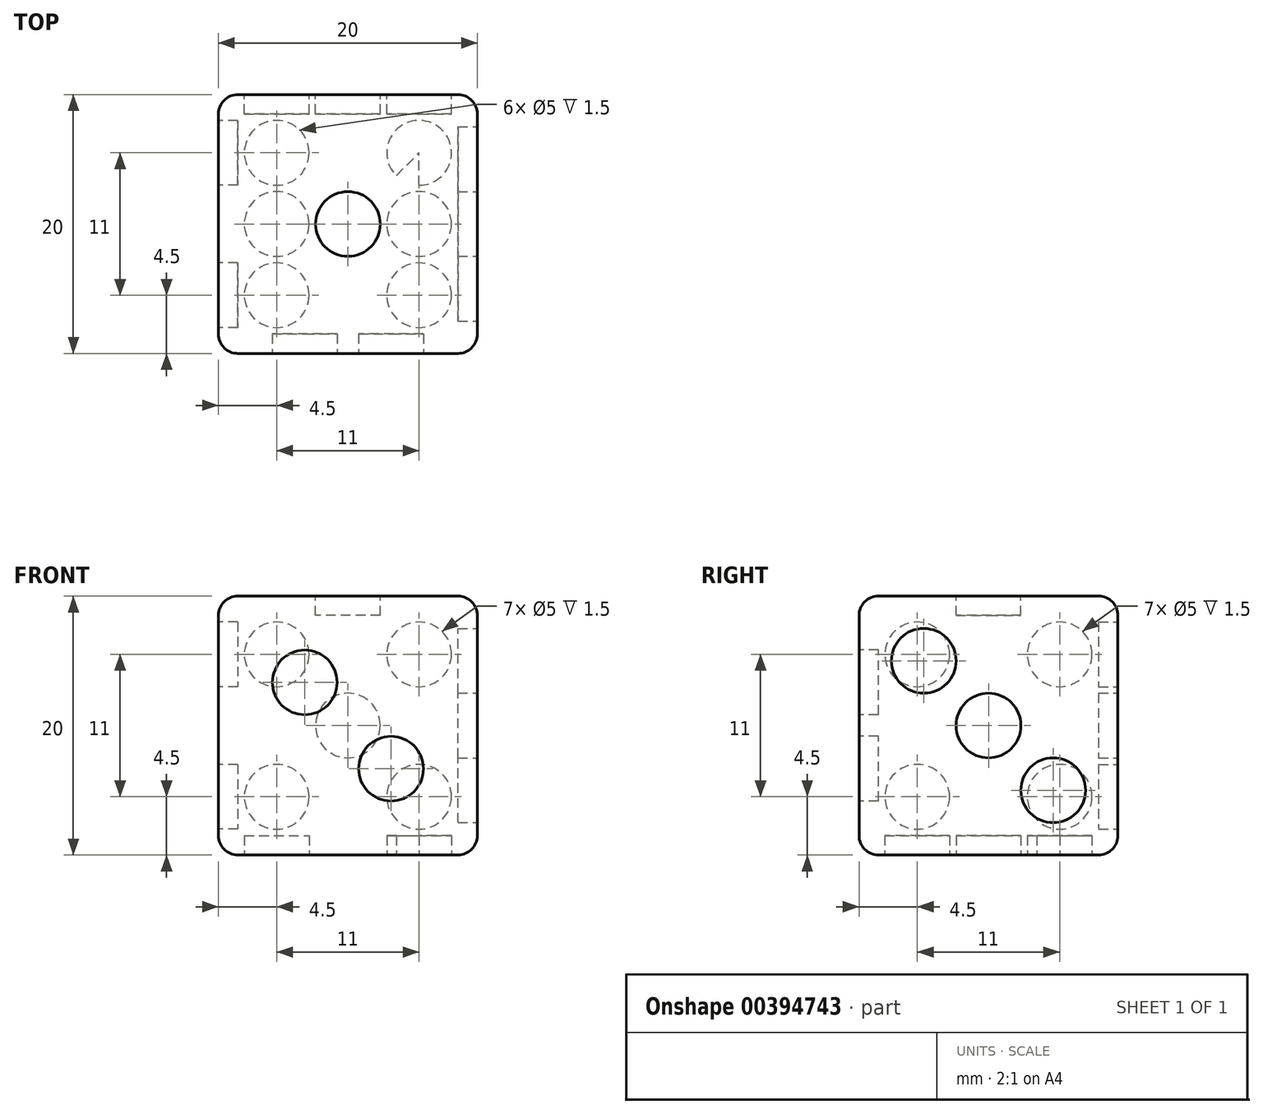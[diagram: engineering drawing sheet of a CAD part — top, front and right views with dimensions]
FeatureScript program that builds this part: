
annotation { "Feature Type Name" : "Feature", "Feature Type Description" : "" }
export const myFeature = defineFeature(function(context is Context, id is Id, definition is map)
    precondition{}
    {
        {
            assignVariable(context, id + "F0", {"name" : "Extrude", "anyValue" : -1.5});
        }
        {
            var Q0;
            Q0=qCreatedBy(makeId("Top.planeOp"),FACE);
            var sketch = newSketch(context, id + "F1", { "sketchPlane" : qUnion([Q0])});
            skLineSegment(sketch, "E0.bottom", {"start": v(-10, 10) * mm, "end": v(10, 10) * mm});
            skLineSegment(sketch, "E0.top", {"start": v(-10, -10) * mm, "end": v(10, -10) * mm});
            skLineSegment(sketch, "E0.left", {"start": v(-10, 10) * mm, "end": v(-10, -10) * mm});
            skLineSegment(sketch, "E0.right", {"start": v(10, 10) * mm, "end": v(10, -10) * mm});
            skPoint(sketch, "E0.middle", {"position": v(0, 0) * mm});
            skSolve(sketch);
        }
        {
            var Q0;
            Q0=makeQuery(id+"F1.imprint","IMPRINT",FACE,{"disambiguationData":[TD([[makeQuery(id+"F1.imprint","IMPRINT",EDGE,{"derivedFrom":sQuery(id+"F1.wireOp",EDGE,"E0.bottom")}),-1.0]])]});
            extrude(context, id + "F2", {"entities" : qUnion([Q0]), "depth" : 20 * mm});
        }
        {
            var Q0;
            Q0=makeQuery(id+"F2.opExtrude","CAP_FACE",FACE,{"disambiguationData":[OSD([sQuery(id+"F1.wireOp",EDGE,"E0.bottom"),sQuery(id+"F1.wireOp",EDGE,"E0.top"),sQuery(id+"F1.wireOp",EDGE,"E0.left"),sQuery(id+"F1.wireOp",EDGE,"E0.right")])],"isStart":false});
            var sketch = newSketch(context, id + "F3", { "sketchPlane" : qUnion([Q0])});
            skCircle(sketch, "E1", {"center": v(0, 0) * mm, "radius": 2.5 * mm});
            skSolve(sketch);
        }
        {
            var Q0;
            Q0=makeQuery(id+"F2.opExtrude","CAP_FACE",FACE,{"disambiguationData":[OSD([sQuery(id+"F1.wireOp",EDGE,"E0.bottom"),sQuery(id+"F1.wireOp",EDGE,"E0.top"),sQuery(id+"F1.wireOp",EDGE,"E0.left"),sQuery(id+"F1.wireOp",EDGE,"E0.right")])],"isStart":true});
            var sketch = newSketch(context, id + "F4", { "sketchPlane" : qUnion([Q0])});
            skCircle(sketch, "E2", {"center": v(-5.5, 5.5) * mm, "radius": 2.5 * mm});
            skCircle(sketch, "E3", {"center": v(-5.5, -5.5) * mm, "radius": 2.5 * mm});
            skCircle(sketch, "E4", {"center": v(-5.5, 0) * mm, "radius": 2.5 * mm});
            skCircle(sketch, "E5", {"center": v(5.5, 5.5) * mm, "radius": 2.5 * mm});
            skCircle(sketch, "E6", {"center": v(5.5, 0) * mm, "radius": 2.5 * mm});
            skCircle(sketch, "E7", {"center": v(5.5, -5.5) * mm, "radius": 2.5 * mm});
            skLineSegment(sketch, "E8", {"start": v(10, 10) * mm, "end": v(-10, -10) * mm});
            skLineSegment(sketch, "E9", {"start": v(-10, 10) * mm, "end": v(10, -10) * mm});
            skLineSegment(sketch, "E10", {"start": v(-5.5, 5.5) * mm, "end": v(-5.5, -5.5) * mm});
            skLineSegment(sketch, "E11", {"start": v(5.5, 5.5) * mm, "end": v(5.5, -5.5) * mm});
            skSolve(sketch);
        }
        {
            var Q0;
            Q0=makeQuery(id+"F2.opExtrude","SWEPT_FACE",FACE,{"disambiguationData":[OSD([sQuery(id+"F1.wireOp",EDGE,"E0.bottom")])]});
            var sketch = newSketch(context, id + "F5", { "sketchPlane" : qUnion([Q0])});
            skLineSegment(sketch, "E12", {"start": v(10, 20) * mm, "end": v(-10, 0) * mm});
            skLineSegment(sketch, "E13", {"start": v(-10, 20) * mm, "end": v(10, 0) * mm});
            skCircle(sketch, "E14", {"center": v(0, 10) * mm, "radius": 2.5 * mm});
            skCircle(sketch, "E15", {"center": v(-5.5, 15.5) * mm, "radius": 2.5 * mm});
            skCircle(sketch, "E16", {"center": v(5.5, 15.5) * mm, "radius": 2.5 * mm});
            skCircle(sketch, "E17", {"center": v(5.5, 4.5) * mm, "radius": 2.5 * mm});
            skCircle(sketch, "E18", {"center": v(-5.5, 4.5) * mm, "radius": 2.5 * mm});
            skLineSegment(sketch, "E19.bottom", {"start": v(-5.5, 15.5) * mm, "end": v(5.5, 15.5) * mm});
            skLineSegment(sketch, "E19.top", {"start": v(-5.5, 4.5) * mm, "end": v(5.5, 4.5) * mm});
            skLineSegment(sketch, "E19.left", {"start": v(-5.5, 15.5) * mm, "end": v(-5.5, 4.5) * mm});
            skLineSegment(sketch, "E19.right", {"start": v(5.5, 15.5) * mm, "end": v(5.5, 4.5) * mm});
            skSolve(sketch);
        }
        {
            var Q0;
            Q0=makeQuery(id+"F2.opExtrude","SWEPT_FACE",FACE,{"disambiguationData":[OSD([sQuery(id+"F1.wireOp",EDGE,"E0.top")])]});
            var sketch = newSketch(context, id + "F6", { "sketchPlane" : qUnion([Q0])});
            skLineSegment(sketch, "E20", {"start": v(-10, 20) * mm, "end": v(-3.33, 13.33) * mm});
            skLineSegment(sketch, "E21", {"start": v(-3.33, 13.33) * mm, "end": v(3.33, 6.67) * mm});
            skLineSegment(sketch, "E22", {"start": v(3.33, 6.67) * mm, "end": v(10, 0) * mm});
            skCircle(sketch, "E23", {"center": v(-3.33, 13.33) * mm, "radius": 2.5 * mm});
            skCircle(sketch, "E24", {"center": v(3.33, 6.67) * mm, "radius": 2.5 * mm});
            skSolve(sketch);
        }
        {
            var Q0;
            Q0=makeQuery(id+"F2.opExtrude","SWEPT_FACE",FACE,{"disambiguationData":[OSD([sQuery(id+"F1.wireOp",EDGE,"E0.left")])]});
            var sketch = newSketch(context, id + "F7", { "sketchPlane" : qUnion([Q0])});
            skLineSegment(sketch, "E25", {"start": v(-10, 20) * mm, "end": v(10, 0) * mm});
            skLineSegment(sketch, "E26", {"start": v(10, 20) * mm, "end": v(-10, 0) * mm});
            skCircle(sketch, "E27", {"center": v(-5.5, 15.5) * mm, "radius": 2.5 * mm});
            skCircle(sketch, "E28", {"center": v(5.5, 15.5) * mm, "radius": 2.5 * mm});
            skCircle(sketch, "E29", {"center": v(5.5, 4.5) * mm, "radius": 2.5 * mm});
            skCircle(sketch, "E30", {"center": v(-5.5, 4.5) * mm, "radius": 2.5 * mm});
            skLineSegment(sketch, "E31.bottom", {"start": v(-5.5, 15.5) * mm, "end": v(5.5, 15.5) * mm});
            skLineSegment(sketch, "E31.top", {"start": v(-5.5, 4.5) * mm, "end": v(5.5, 4.5) * mm});
            skLineSegment(sketch, "E31.left", {"start": v(-5.5, 15.5) * mm, "end": v(-5.5, 4.5) * mm});
            skLineSegment(sketch, "E31.right", {"start": v(5.5, 15.5) * mm, "end": v(5.5, 4.5) * mm});
            skSolve(sketch);
        }
        {
            var Q0;
            Q0=makeQuery(id+"F2.opExtrude","SWEPT_FACE",FACE,{"disambiguationData":[OSD([sQuery(id+"F1.wireOp",EDGE,"E0.right")])]});
            var sketch = newSketch(context, id + "F8", { "sketchPlane" : qUnion([Q0])});
            skLineSegment(sketch, "E32", {"start": v(-10, 20) * mm, "end": v(-5, 15) * mm});
            skLineSegment(sketch, "E33", {"start": v(-5, 15) * mm, "end": v(0, 10) * mm});
            skLineSegment(sketch, "E34", {"start": v(0, 10) * mm, "end": v(5, 5) * mm});
            skLineSegment(sketch, "E35", {"start": v(5, 5) * mm, "end": v(10, 0) * mm});
            skCircle(sketch, "E36", {"center": v(-5, 15) * mm, "radius": 2.5 * mm});
            skCircle(sketch, "E37", {"center": v(0, 10) * mm, "radius": 2.5 * mm});
            skCircle(sketch, "E38", {"center": v(5, 5) * mm, "radius": 2.5 * mm});
            skSolve(sketch);
        }
        {
            var Q0;
            Q0=makeQuery(id+"F3.imprint","IMPRINT",FACE,{"disambiguationData":[TD([[makeQuery(id+"F3.imprint","IMPRINT",EDGE,{"derivedFrom":sQuery(id+"F3.wireOp",EDGE,"E1")}),1.0]])]});
            extrude(context, id + "F9", {"entities" : qUnion([Q0]), "operationType" : NewBodyOperationType.REMOVE, "depth" : (getVariable(context, 'Extrude')) * mm});
        }
        {
            var Q0;
            {var subQ0=sQuery(id+"F6.wireOp",EDGE,"E21");var subQ1=sQuery(id+"F6.wireOp",EDGE,"E20");var subQ2=makeQuery(id+"F6.imprint","INTERSECT",VERTEX,{"derivedFrom":[subQ1,subQ0]});Q0=makeQuery(id+"F6.imprint","IMPRINT",FACE,{"disambiguationData":[TD([[makeQuery(id+"F6.imprint","IMPRINT",EDGE,{"disambiguationData":[TD([[subQ2,1.0]])],"derivedFrom":subQ1}),1.0]])]});}
            var Q1;
            {var subQ0=sQuery(id+"F6.wireOp",EDGE,"E21");var subQ1=sQuery(id+"F6.wireOp",EDGE,"E20");var subQ2=makeQuery(id+"F6.imprint","INTERSECT",VERTEX,{"derivedFrom":[subQ1,subQ0]});Q1=makeQuery(id+"F6.imprint","IMPRINT",FACE,{"disambiguationData":[TD([[makeQuery(id+"F6.imprint","IMPRINT",EDGE,{"disambiguationData":[TD([[subQ2,1.0]])],"derivedFrom":subQ1}),-1.0]])]});}
            var Q2;
            {var subQ0=sQuery(id+"F6.wireOp",EDGE,"E22");var subQ1=sQuery(id+"F6.wireOp",EDGE,"E21");var subQ2=makeQuery(id+"F6.imprint","INTERSECT",VERTEX,{"derivedFrom":[subQ1,subQ0]});Q2=makeQuery(id+"F6.imprint","IMPRINT",FACE,{"disambiguationData":[TD([[makeQuery(id+"F6.imprint","IMPRINT",EDGE,{"disambiguationData":[TD([[subQ2,1.0]])],"derivedFrom":subQ1}),-1.0]])]});}
            var Q3;
            {var subQ0=sQuery(id+"F6.wireOp",EDGE,"E22");var subQ1=sQuery(id+"F6.wireOp",EDGE,"E21");var subQ2=makeQuery(id+"F6.imprint","INTERSECT",VERTEX,{"derivedFrom":[subQ1,subQ0]});Q3=makeQuery(id+"F6.imprint","IMPRINT",FACE,{"disambiguationData":[TD([[makeQuery(id+"F6.imprint","IMPRINT",EDGE,{"disambiguationData":[TD([[subQ2,1.0]])],"derivedFrom":subQ1}),1.0]])]});}
            extrude(context, id + "F10", {"entities" : qUnion([Q0, Q1, Q2, Q3]), "operationType" : NewBodyOperationType.REMOVE, "depth" : (getVariable(context, 'Extrude')) * mm});
        }
        {
            var Q0;
            {var subQ0=sQuery(id+"F8.wireOp",EDGE,"E33");var subQ1=sQuery(id+"F8.wireOp",EDGE,"E32");var subQ2=makeQuery(id+"F8.imprint","INTERSECT",VERTEX,{"derivedFrom":[subQ1,subQ0]});Q0=makeQuery(id+"F8.imprint","IMPRINT",FACE,{"disambiguationData":[TD([[makeQuery(id+"F8.imprint","IMPRINT",EDGE,{"disambiguationData":[TD([[subQ2,1.0]])],"derivedFrom":subQ1}),1.0]])]});}
            var Q1;
            {var subQ0=sQuery(id+"F8.wireOp",EDGE,"E33");var subQ1=sQuery(id+"F8.wireOp",EDGE,"E32");var subQ2=makeQuery(id+"F8.imprint","INTERSECT",VERTEX,{"derivedFrom":[subQ1,subQ0]});Q1=makeQuery(id+"F8.imprint","IMPRINT",FACE,{"disambiguationData":[TD([[makeQuery(id+"F8.imprint","IMPRINT",EDGE,{"disambiguationData":[TD([[subQ2,1.0]])],"derivedFrom":subQ1}),-1.0]])]});}
            var Q2;
            {var subQ0=sQuery(id+"F8.wireOp",EDGE,"E34");var subQ1=sQuery(id+"F8.wireOp",EDGE,"E33");var subQ2=makeQuery(id+"F8.imprint","INTERSECT",VERTEX,{"derivedFrom":[subQ1,subQ0]});Q2=makeQuery(id+"F8.imprint","IMPRINT",FACE,{"disambiguationData":[TD([[makeQuery(id+"F8.imprint","IMPRINT",EDGE,{"disambiguationData":[TD([[subQ2,1.0]])],"derivedFrom":subQ1}),-1.0]])]});}
            var Q3;
            {var subQ0=sQuery(id+"F8.wireOp",EDGE,"E34");var subQ1=sQuery(id+"F8.wireOp",EDGE,"E33");var subQ2=makeQuery(id+"F8.imprint","INTERSECT",VERTEX,{"derivedFrom":[subQ1,subQ0]});Q3=makeQuery(id+"F8.imprint","IMPRINT",FACE,{"disambiguationData":[TD([[makeQuery(id+"F8.imprint","IMPRINT",EDGE,{"disambiguationData":[TD([[subQ2,1.0]])],"derivedFrom":subQ1}),1.0]])]});}
            var Q4;
            {var subQ0=sQuery(id+"F8.wireOp",EDGE,"E35");var subQ1=sQuery(id+"F8.wireOp",EDGE,"E34");var subQ2=makeQuery(id+"F8.imprint","INTERSECT",VERTEX,{"derivedFrom":[subQ1,subQ0]});Q4=makeQuery(id+"F8.imprint","IMPRINT",FACE,{"disambiguationData":[TD([[makeQuery(id+"F8.imprint","IMPRINT",EDGE,{"disambiguationData":[TD([[subQ2,1.0]])],"derivedFrom":subQ1}),1.0]])]});}
            var Q5;
            {var subQ0=sQuery(id+"F8.wireOp",EDGE,"E35");var subQ1=sQuery(id+"F8.wireOp",EDGE,"E34");var subQ2=makeQuery(id+"F8.imprint","INTERSECT",VERTEX,{"derivedFrom":[subQ1,subQ0]});Q5=makeQuery(id+"F8.imprint","IMPRINT",FACE,{"disambiguationData":[TD([[makeQuery(id+"F8.imprint","IMPRINT",EDGE,{"disambiguationData":[TD([[subQ2,1.0]])],"derivedFrom":subQ1}),-1.0]])]});}
            extrude(context, id + "F11", {"entities" : qUnion([Q0, Q1, Q2, Q3, Q4, Q5]), "operationType" : NewBodyOperationType.REMOVE, "depth" : (getVariable(context, 'Extrude')) * mm});
        }
        {
            var Q0;
            {var subQ1=sQuery(id+"F7.wireOp",EDGE,"E25");var subQ3=sQuery(id+"F7.wireOp",EDGE,"E29");var subQ4=makeQuery(id+"F7.imprint","INTERSECT",VERTEX,{"disambiguationData":[OD(1.0)],"derivedFrom":[subQ1,subQ3]});Q0=makeQuery(id+"F7.imprint","IMPRINT",FACE,{"disambiguationData":[TD([[makeQuery(id+"F7.imprint","IMPRINT",EDGE,{"disambiguationData":[TD([[subQ4,1.0]])],"derivedFrom":subQ3}),1.0]])]});}
            var Q1;
            {var subQ1=sQuery(id+"F7.wireOp",EDGE,"E25");var subQ3=sQuery(id+"F7.wireOp",EDGE,"E29");var subQ4=makeQuery(id+"F7.imprint","INTERSECT",VERTEX,{"disambiguationData":[OD(0.0)],"derivedFrom":[subQ1,subQ3]});Q1=makeQuery(id+"F7.imprint","IMPRINT",FACE,{"disambiguationData":[TD([[makeQuery(id+"F7.imprint","IMPRINT",EDGE,{"disambiguationData":[TD([[subQ4,-1.0]])],"derivedFrom":subQ3}),1.0]])]});}
            var Q2;
            {var subQ1=sQuery(id+"F7.wireOp",EDGE,"E25");var subQ3=sQuery(id+"F7.wireOp",EDGE,"E29");var subQ4=makeQuery(id+"F7.imprint","INTERSECT",VERTEX,{"disambiguationData":[OD(0.0)],"derivedFrom":[subQ1,subQ3]});Q2=makeQuery(id+"F7.imprint","IMPRINT",FACE,{"disambiguationData":[TD([[makeQuery(id+"F7.imprint","IMPRINT",EDGE,{"disambiguationData":[TD([[subQ4,1.0]])],"derivedFrom":subQ3}),1.0]])]});}
            var Q3;
            {var subQ1=sQuery(id+"F7.wireOp",EDGE,"E25");var subQ3=sQuery(id+"F7.wireOp",EDGE,"E29");var subQ4=makeQuery(id+"F7.imprint","INTERSECT",VERTEX,{"disambiguationData":[OD(1.0)],"derivedFrom":[subQ1,subQ3]});Q3=makeQuery(id+"F7.imprint","IMPRINT",FACE,{"disambiguationData":[TD([[makeQuery(id+"F7.imprint","IMPRINT",EDGE,{"disambiguationData":[TD([[subQ4,-1.0]])],"derivedFrom":subQ3}),1.0]])]});}
            var Q4;
            {var subQ1=sQuery(id+"F7.wireOp",EDGE,"E26");var subQ3=sQuery(id+"F7.wireOp",EDGE,"E30");var subQ4=makeQuery(id+"F7.imprint","INTERSECT",VERTEX,{"disambiguationData":[OD(1.0)],"derivedFrom":[subQ1,subQ3]});Q4=makeQuery(id+"F7.imprint","IMPRINT",FACE,{"disambiguationData":[TD([[makeQuery(id+"F7.imprint","IMPRINT",EDGE,{"disambiguationData":[TD([[subQ4,1.0]])],"derivedFrom":subQ3}),1.0]])]});}
            var Q5;
            {var subQ1=sQuery(id+"F7.wireOp",EDGE,"E26");var subQ3=sQuery(id+"F7.wireOp",EDGE,"E30");var subQ4=makeQuery(id+"F7.imprint","INTERSECT",VERTEX,{"disambiguationData":[OD(1.0)],"derivedFrom":[subQ1,subQ3]});Q5=makeQuery(id+"F7.imprint","IMPRINT",FACE,{"disambiguationData":[TD([[makeQuery(id+"F7.imprint","IMPRINT",EDGE,{"disambiguationData":[TD([[subQ4,-1.0]])],"derivedFrom":subQ3}),1.0]])]});}
            var Q6;
            {var subQ1=sQuery(id+"F7.wireOp",EDGE,"E26");var subQ3=sQuery(id+"F7.wireOp",EDGE,"E30");var subQ4=makeQuery(id+"F7.imprint","INTERSECT",VERTEX,{"disambiguationData":[OD(0.0)],"derivedFrom":[subQ1,subQ3]});Q6=makeQuery(id+"F7.imprint","IMPRINT",FACE,{"disambiguationData":[TD([[makeQuery(id+"F7.imprint","IMPRINT",EDGE,{"disambiguationData":[TD([[subQ4,1.0]])],"derivedFrom":subQ3}),1.0]])]});}
            var Q7;
            {var subQ1=sQuery(id+"F7.wireOp",EDGE,"E26");var subQ3=sQuery(id+"F7.wireOp",EDGE,"E30");var subQ4=makeQuery(id+"F7.imprint","INTERSECT",VERTEX,{"disambiguationData":[OD(0.0)],"derivedFrom":[subQ1,subQ3]});Q7=makeQuery(id+"F7.imprint","IMPRINT",FACE,{"disambiguationData":[TD([[makeQuery(id+"F7.imprint","IMPRINT",EDGE,{"disambiguationData":[TD([[subQ4,-1.0]])],"derivedFrom":subQ3}),1.0]])]});}
            var Q8;
            {var subQ1=sQuery(id+"F7.wireOp",EDGE,"E25");var subQ3=sQuery(id+"F7.wireOp",EDGE,"E27");var subQ4=makeQuery(id+"F7.imprint","INTERSECT",VERTEX,{"disambiguationData":[OD(1.0)],"derivedFrom":[subQ1,subQ3]});Q8=makeQuery(id+"F7.imprint","IMPRINT",FACE,{"disambiguationData":[TD([[makeQuery(id+"F7.imprint","IMPRINT",EDGE,{"disambiguationData":[TD([[subQ4,1.0]])],"derivedFrom":subQ3}),1.0]])]});}
            var Q9;
            {var subQ1=sQuery(id+"F7.wireOp",EDGE,"E25");var subQ3=sQuery(id+"F7.wireOp",EDGE,"E27");var subQ4=makeQuery(id+"F7.imprint","INTERSECT",VERTEX,{"disambiguationData":[OD(0.0)],"derivedFrom":[subQ1,subQ3]});Q9=makeQuery(id+"F7.imprint","IMPRINT",FACE,{"disambiguationData":[TD([[makeQuery(id+"F7.imprint","IMPRINT",EDGE,{"disambiguationData":[TD([[subQ4,-1.0]])],"derivedFrom":subQ3}),1.0]])]});}
            var Q10;
            {var subQ1=sQuery(id+"F7.wireOp",EDGE,"E25");var subQ3=sQuery(id+"F7.wireOp",EDGE,"E27");var subQ4=makeQuery(id+"F7.imprint","INTERSECT",VERTEX,{"disambiguationData":[OD(0.0)],"derivedFrom":[subQ1,subQ3]});Q10=makeQuery(id+"F7.imprint","IMPRINT",FACE,{"disambiguationData":[TD([[makeQuery(id+"F7.imprint","IMPRINT",EDGE,{"disambiguationData":[TD([[subQ4,1.0]])],"derivedFrom":subQ3}),1.0]])]});}
            var Q11;
            {var subQ1=sQuery(id+"F7.wireOp",EDGE,"E25");var subQ3=sQuery(id+"F7.wireOp",EDGE,"E27");var subQ4=makeQuery(id+"F7.imprint","INTERSECT",VERTEX,{"disambiguationData":[OD(1.0)],"derivedFrom":[subQ1,subQ3]});Q11=makeQuery(id+"F7.imprint","IMPRINT",FACE,{"disambiguationData":[TD([[makeQuery(id+"F7.imprint","IMPRINT",EDGE,{"disambiguationData":[TD([[subQ4,-1.0]])],"derivedFrom":subQ3}),1.0]])]});}
            var Q12;
            {var subQ1=sQuery(id+"F7.wireOp",EDGE,"E26");var subQ3=sQuery(id+"F7.wireOp",EDGE,"E28");var subQ4=makeQuery(id+"F7.imprint","INTERSECT",VERTEX,{"disambiguationData":[OD(1.0)],"derivedFrom":[subQ1,subQ3]});Q12=makeQuery(id+"F7.imprint","IMPRINT",FACE,{"disambiguationData":[TD([[makeQuery(id+"F7.imprint","IMPRINT",EDGE,{"disambiguationData":[TD([[subQ4,-1.0]])],"derivedFrom":subQ3}),1.0]])]});}
            var Q13;
            {var subQ1=sQuery(id+"F7.wireOp",EDGE,"E26");var subQ3=sQuery(id+"F7.wireOp",EDGE,"E28");var subQ4=makeQuery(id+"F7.imprint","INTERSECT",VERTEX,{"disambiguationData":[OD(0.0)],"derivedFrom":[subQ1,subQ3]});Q13=makeQuery(id+"F7.imprint","IMPRINT",FACE,{"disambiguationData":[TD([[makeQuery(id+"F7.imprint","IMPRINT",EDGE,{"disambiguationData":[TD([[subQ4,1.0]])],"derivedFrom":subQ3}),1.0]])]});}
            var Q14;
            {var subQ1=sQuery(id+"F7.wireOp",EDGE,"E26");var subQ3=sQuery(id+"F7.wireOp",EDGE,"E28");var subQ4=makeQuery(id+"F7.imprint","INTERSECT",VERTEX,{"disambiguationData":[OD(1.0)],"derivedFrom":[subQ1,subQ3]});Q14=makeQuery(id+"F7.imprint","IMPRINT",FACE,{"disambiguationData":[TD([[makeQuery(id+"F7.imprint","IMPRINT",EDGE,{"disambiguationData":[TD([[subQ4,1.0]])],"derivedFrom":subQ3}),1.0]])]});}
            var Q15;
            {var subQ1=sQuery(id+"F7.wireOp",EDGE,"E26");var subQ3=sQuery(id+"F7.wireOp",EDGE,"E28");var subQ4=makeQuery(id+"F7.imprint","INTERSECT",VERTEX,{"disambiguationData":[OD(0.0)],"derivedFrom":[subQ1,subQ3]});Q15=makeQuery(id+"F7.imprint","IMPRINT",FACE,{"disambiguationData":[TD([[makeQuery(id+"F7.imprint","IMPRINT",EDGE,{"disambiguationData":[TD([[subQ4,-1.0]])],"derivedFrom":subQ3}),1.0]])]});}
            extrude(context, id + "F12", {"entities" : qUnion([Q0, Q1, Q2, Q3, Q4, Q5, Q6, Q7, Q8, Q9, Q10, Q11, Q12, Q13, Q14, Q15]), "operationType" : NewBodyOperationType.REMOVE, "depth" : (getVariable(context, 'Extrude')) * mm});
        }
        {
            var Q0;
            {var subQ1=sQuery(id+"F5.wireOp",EDGE,"E12");var subQ3=sQuery(id+"F5.wireOp",EDGE,"E18");var subQ4=makeQuery(id+"F5.imprint","INTERSECT",VERTEX,{"disambiguationData":[OD(1.0)],"derivedFrom":[subQ1,subQ3]});Q0=makeQuery(id+"F5.imprint","IMPRINT",FACE,{"disambiguationData":[TD([[makeQuery(id+"F5.imprint","IMPRINT",EDGE,{"disambiguationData":[TD([[subQ4,1.0]])],"derivedFrom":subQ3}),1.0]])]});}
            var Q1;
            {var subQ1=sQuery(id+"F5.wireOp",EDGE,"E12");var subQ3=sQuery(id+"F5.wireOp",EDGE,"E18");var subQ4=makeQuery(id+"F5.imprint","INTERSECT",VERTEX,{"disambiguationData":[OD(1.0)],"derivedFrom":[subQ1,subQ3]});Q1=makeQuery(id+"F5.imprint","IMPRINT",FACE,{"disambiguationData":[TD([[makeQuery(id+"F5.imprint","IMPRINT",EDGE,{"disambiguationData":[TD([[subQ4,-1.0]])],"derivedFrom":subQ3}),1.0]])]});}
            var Q2;
            {var subQ1=sQuery(id+"F5.wireOp",EDGE,"E12");var subQ3=sQuery(id+"F5.wireOp",EDGE,"E18");var subQ4=makeQuery(id+"F5.imprint","INTERSECT",VERTEX,{"disambiguationData":[OD(0.0)],"derivedFrom":[subQ1,subQ3]});Q2=makeQuery(id+"F5.imprint","IMPRINT",FACE,{"disambiguationData":[TD([[makeQuery(id+"F5.imprint","IMPRINT",EDGE,{"disambiguationData":[TD([[subQ4,1.0]])],"derivedFrom":subQ3}),1.0]])]});}
            var Q3;
            {var subQ1=sQuery(id+"F5.wireOp",EDGE,"E12");var subQ3=sQuery(id+"F5.wireOp",EDGE,"E18");var subQ4=makeQuery(id+"F5.imprint","INTERSECT",VERTEX,{"disambiguationData":[OD(0.0)],"derivedFrom":[subQ1,subQ3]});Q3=makeQuery(id+"F5.imprint","IMPRINT",FACE,{"disambiguationData":[TD([[makeQuery(id+"F5.imprint","IMPRINT",EDGE,{"disambiguationData":[TD([[subQ4,-1.0]])],"derivedFrom":subQ3}),1.0]])]});}
            var Q4;
            {var subQ0=sQuery(id+"F5.wireOp",EDGE,"E13");var subQ1=sQuery(id+"F5.wireOp",EDGE,"E12");var subQ2=makeQuery(id+"F5.imprint","INTERSECT",VERTEX,{"derivedFrom":[subQ1,subQ0]});Q4=makeQuery(id+"F5.imprint","IMPRINT",FACE,{"disambiguationData":[TD([[makeQuery(id+"F5.imprint","IMPRINT",EDGE,{"disambiguationData":[TD([[subQ2,-1.0]])],"derivedFrom":subQ1}),1.0]])]});}
            var Q5;
            {var subQ0=sQuery(id+"F5.wireOp",EDGE,"E14");var subQ1=sQuery(id+"F5.wireOp",EDGE,"E12");var subQ2=makeQuery(id+"F5.imprint","INTERSECT",VERTEX,{"disambiguationData":[OD(0.0)],"derivedFrom":[subQ1,subQ0]});Q5=makeQuery(id+"F5.imprint","IMPRINT",FACE,{"disambiguationData":[TD([[makeQuery(id+"F5.imprint","IMPRINT",EDGE,{"disambiguationData":[TD([[subQ2,-1.0]])],"derivedFrom":subQ1}),1.0]])]});}
            var Q6;
            {var subQ0=sQuery(id+"F5.wireOp",EDGE,"E14");var subQ1=sQuery(id+"F5.wireOp",EDGE,"E12");var subQ2=makeQuery(id+"F5.imprint","INTERSECT",VERTEX,{"disambiguationData":[OD(0.0)],"derivedFrom":[subQ1,subQ0]});Q6=makeQuery(id+"F5.imprint","IMPRINT",FACE,{"disambiguationData":[TD([[makeQuery(id+"F5.imprint","IMPRINT",EDGE,{"disambiguationData":[TD([[subQ2,-1.0]])],"derivedFrom":subQ1}),-1.0]])]});}
            var Q7;
            {var subQ0=sQuery(id+"F5.wireOp",EDGE,"E13");var subQ1=sQuery(id+"F5.wireOp",EDGE,"E12");var subQ2=makeQuery(id+"F5.imprint","INTERSECT",VERTEX,{"derivedFrom":[subQ1,subQ0]});Q7=makeQuery(id+"F5.imprint","IMPRINT",FACE,{"disambiguationData":[TD([[makeQuery(id+"F5.imprint","IMPRINT",EDGE,{"disambiguationData":[TD([[subQ2,-1.0]])],"derivedFrom":subQ1}),-1.0]])]});}
            var Q8;
            {var subQ1=sQuery(id+"F5.wireOp",EDGE,"E13");var subQ3=sQuery(id+"F5.wireOp",EDGE,"E17");var subQ4=makeQuery(id+"F5.imprint","INTERSECT",VERTEX,{"disambiguationData":[OD(0.0)],"derivedFrom":[subQ1,subQ3]});Q8=makeQuery(id+"F5.imprint","IMPRINT",FACE,{"disambiguationData":[TD([[makeQuery(id+"F5.imprint","IMPRINT",EDGE,{"disambiguationData":[TD([[subQ4,-1.0]])],"derivedFrom":subQ3}),1.0]])]});}
            var Q9;
            {var subQ1=sQuery(id+"F5.wireOp",EDGE,"E13");var subQ3=sQuery(id+"F5.wireOp",EDGE,"E17");var subQ4=makeQuery(id+"F5.imprint","INTERSECT",VERTEX,{"disambiguationData":[OD(1.0)],"derivedFrom":[subQ1,subQ3]});Q9=makeQuery(id+"F5.imprint","IMPRINT",FACE,{"disambiguationData":[TD([[makeQuery(id+"F5.imprint","IMPRINT",EDGE,{"disambiguationData":[TD([[subQ4,1.0]])],"derivedFrom":subQ3}),1.0]])]});}
            var Q10;
            {var subQ1=sQuery(id+"F5.wireOp",EDGE,"E13");var subQ3=sQuery(id+"F5.wireOp",EDGE,"E17");var subQ4=makeQuery(id+"F5.imprint","INTERSECT",VERTEX,{"disambiguationData":[OD(1.0)],"derivedFrom":[subQ1,subQ3]});Q10=makeQuery(id+"F5.imprint","IMPRINT",FACE,{"disambiguationData":[TD([[makeQuery(id+"F5.imprint","IMPRINT",EDGE,{"disambiguationData":[TD([[subQ4,-1.0]])],"derivedFrom":subQ3}),1.0]])]});}
            var Q11;
            {var subQ1=sQuery(id+"F5.wireOp",EDGE,"E13");var subQ3=sQuery(id+"F5.wireOp",EDGE,"E17");var subQ4=makeQuery(id+"F5.imprint","INTERSECT",VERTEX,{"disambiguationData":[OD(0.0)],"derivedFrom":[subQ1,subQ3]});Q11=makeQuery(id+"F5.imprint","IMPRINT",FACE,{"disambiguationData":[TD([[makeQuery(id+"F5.imprint","IMPRINT",EDGE,{"disambiguationData":[TD([[subQ4,1.0]])],"derivedFrom":subQ3}),1.0]])]});}
            var Q12;
            {var subQ1=sQuery(id+"F5.wireOp",EDGE,"E12");var subQ3=sQuery(id+"F5.wireOp",EDGE,"E16");var subQ4=makeQuery(id+"F5.imprint","INTERSECT",VERTEX,{"disambiguationData":[OD(1.0)],"derivedFrom":[subQ1,subQ3]});Q12=makeQuery(id+"F5.imprint","IMPRINT",FACE,{"disambiguationData":[TD([[makeQuery(id+"F5.imprint","IMPRINT",EDGE,{"disambiguationData":[TD([[subQ4,-1.0]])],"derivedFrom":subQ3}),1.0]])]});}
            var Q13;
            {var subQ1=sQuery(id+"F5.wireOp",EDGE,"E12");var subQ3=sQuery(id+"F5.wireOp",EDGE,"E16");var subQ4=makeQuery(id+"F5.imprint","INTERSECT",VERTEX,{"disambiguationData":[OD(0.0)],"derivedFrom":[subQ1,subQ3]});Q13=makeQuery(id+"F5.imprint","IMPRINT",FACE,{"disambiguationData":[TD([[makeQuery(id+"F5.imprint","IMPRINT",EDGE,{"disambiguationData":[TD([[subQ4,1.0]])],"derivedFrom":subQ3}),1.0]])]});}
            var Q14;
            {var subQ1=sQuery(id+"F5.wireOp",EDGE,"E12");var subQ3=sQuery(id+"F5.wireOp",EDGE,"E16");var subQ4=makeQuery(id+"F5.imprint","INTERSECT",VERTEX,{"disambiguationData":[OD(1.0)],"derivedFrom":[subQ1,subQ3]});Q14=makeQuery(id+"F5.imprint","IMPRINT",FACE,{"disambiguationData":[TD([[makeQuery(id+"F5.imprint","IMPRINT",EDGE,{"disambiguationData":[TD([[subQ4,1.0]])],"derivedFrom":subQ3}),1.0]])]});}
            var Q15;
            {var subQ1=sQuery(id+"F5.wireOp",EDGE,"E12");var subQ3=sQuery(id+"F5.wireOp",EDGE,"E16");var subQ4=makeQuery(id+"F5.imprint","INTERSECT",VERTEX,{"disambiguationData":[OD(0.0)],"derivedFrom":[subQ1,subQ3]});Q15=makeQuery(id+"F5.imprint","IMPRINT",FACE,{"disambiguationData":[TD([[makeQuery(id+"F5.imprint","IMPRINT",EDGE,{"disambiguationData":[TD([[subQ4,-1.0]])],"derivedFrom":subQ3}),1.0]])]});}
            var Q16;
            {var subQ1=sQuery(id+"F5.wireOp",EDGE,"E13");var subQ3=sQuery(id+"F5.wireOp",EDGE,"E15");var subQ4=makeQuery(id+"F5.imprint","INTERSECT",VERTEX,{"disambiguationData":[OD(1.0)],"derivedFrom":[subQ1,subQ3]});Q16=makeQuery(id+"F5.imprint","IMPRINT",FACE,{"disambiguationData":[TD([[makeQuery(id+"F5.imprint","IMPRINT",EDGE,{"disambiguationData":[TD([[subQ4,-1.0]])],"derivedFrom":subQ3}),1.0]])]});}
            var Q17;
            {var subQ1=sQuery(id+"F5.wireOp",EDGE,"E13");var subQ3=sQuery(id+"F5.wireOp",EDGE,"E15");var subQ4=makeQuery(id+"F5.imprint","INTERSECT",VERTEX,{"disambiguationData":[OD(1.0)],"derivedFrom":[subQ1,subQ3]});Q17=makeQuery(id+"F5.imprint","IMPRINT",FACE,{"disambiguationData":[TD([[makeQuery(id+"F5.imprint","IMPRINT",EDGE,{"disambiguationData":[TD([[subQ4,1.0]])],"derivedFrom":subQ3}),1.0]])]});}
            var Q18;
            {var subQ1=sQuery(id+"F5.wireOp",EDGE,"E13");var subQ3=sQuery(id+"F5.wireOp",EDGE,"E15");var subQ4=makeQuery(id+"F5.imprint","INTERSECT",VERTEX,{"disambiguationData":[OD(0.0)],"derivedFrom":[subQ1,subQ3]});Q18=makeQuery(id+"F5.imprint","IMPRINT",FACE,{"disambiguationData":[TD([[makeQuery(id+"F5.imprint","IMPRINT",EDGE,{"disambiguationData":[TD([[subQ4,-1.0]])],"derivedFrom":subQ3}),1.0]])]});}
            var Q19;
            {var subQ1=sQuery(id+"F5.wireOp",EDGE,"E13");var subQ3=sQuery(id+"F5.wireOp",EDGE,"E15");var subQ4=makeQuery(id+"F5.imprint","INTERSECT",VERTEX,{"disambiguationData":[OD(0.0)],"derivedFrom":[subQ1,subQ3]});Q19=makeQuery(id+"F5.imprint","IMPRINT",FACE,{"disambiguationData":[TD([[makeQuery(id+"F5.imprint","IMPRINT",EDGE,{"disambiguationData":[TD([[subQ4,1.0]])],"derivedFrom":subQ3}),1.0]])]});}
            extrude(context, id + "F13", {"entities" : qUnion([Q0, Q1, Q2, Q3, Q4, Q5, Q6, Q7, Q8, Q9, Q10, Q11, Q12, Q13, Q14, Q15, Q16, Q17, Q18, Q19]), "operationType" : NewBodyOperationType.REMOVE, "depth" : (getVariable(context, 'Extrude')) * mm});
        }
        {
            var Q0;
            {var subQ0=sQuery(id+"F4.wireOp",EDGE,"E9");var subQ1=sQuery(id+"F4.wireOp",EDGE,"E7");var subQ2=makeQuery(id+"F4.imprint","INTERSECT",VERTEX,{"disambiguationData":[OD(0.0)],"derivedFrom":[subQ1,subQ0]});Q0=makeQuery(id+"F4.imprint","IMPRINT",FACE,{"disambiguationData":[TD([[makeQuery(id+"F4.imprint","IMPRINT",EDGE,{"disambiguationData":[TD([[subQ2,-1.0]])],"derivedFrom":subQ1}),1.0]])]});}
            var Q1;
            {var subQ0=sQuery(id+"F4.wireOp",EDGE,"E11");var subQ1=sQuery(id+"F4.wireOp",EDGE,"E7");var subQ2=makeQuery(id+"F4.imprint","INTERSECT",VERTEX,{"derivedFrom":[subQ1,subQ0]});Q1=makeQuery(id+"F4.imprint","IMPRINT",FACE,{"disambiguationData":[TD([[makeQuery(id+"F4.imprint","IMPRINT",EDGE,{"disambiguationData":[TD([[subQ2,1.0]])],"derivedFrom":subQ1}),1.0]])]});}
            var Q2;
            {var subQ0=sQuery(id+"F4.wireOp",EDGE,"E9");var subQ1=sQuery(id+"F4.wireOp",EDGE,"E7");var subQ2=makeQuery(id+"F4.imprint","INTERSECT",VERTEX,{"disambiguationData":[OD(0.0)],"derivedFrom":[subQ1,subQ0]});Q2=makeQuery(id+"F4.imprint","IMPRINT",FACE,{"disambiguationData":[TD([[makeQuery(id+"F4.imprint","IMPRINT",EDGE,{"disambiguationData":[TD([[subQ2,1.0]])],"derivedFrom":subQ1}),1.0]])]});}
            var Q3;
            {var subQ0=sQuery(id+"F4.wireOp",EDGE,"E11");var subQ1=sQuery(id+"F4.wireOp",EDGE,"E6");var subQ2=makeQuery(id+"F4.imprint","INTERSECT",VERTEX,{"disambiguationData":[OD(0.0)],"derivedFrom":[subQ1,subQ0]});Q3=makeQuery(id+"F4.imprint","IMPRINT",FACE,{"disambiguationData":[TD([[makeQuery(id+"F4.imprint","IMPRINT",EDGE,{"disambiguationData":[TD([[subQ2,1.0]])],"derivedFrom":subQ1}),1.0]])]});}
            var Q4;
            {var subQ0=sQuery(id+"F4.wireOp",EDGE,"E11");var subQ1=sQuery(id+"F4.wireOp",EDGE,"E6");var subQ2=makeQuery(id+"F4.imprint","INTERSECT",VERTEX,{"disambiguationData":[OD(0.0)],"derivedFrom":[subQ1,subQ0]});Q4=makeQuery(id+"F4.imprint","IMPRINT",FACE,{"disambiguationData":[TD([[makeQuery(id+"F4.imprint","IMPRINT",EDGE,{"disambiguationData":[TD([[subQ2,-1.0]])],"derivedFrom":subQ1}),1.0]])]});}
            var Q5;
            {var subQ0=sQuery(id+"F4.wireOp",EDGE,"E8");var subQ1=sQuery(id+"F4.wireOp",EDGE,"E5");var subQ2=makeQuery(id+"F4.imprint","INTERSECT",VERTEX,{"disambiguationData":[OD(1.0)],"derivedFrom":[subQ1,subQ0]});Q5=makeQuery(id+"F4.imprint","IMPRINT",FACE,{"disambiguationData":[TD([[makeQuery(id+"F4.imprint","IMPRINT",EDGE,{"disambiguationData":[TD([[subQ2,1.0]])],"derivedFrom":subQ1}),1.0]])]});}
            var Q6;
            {var subQ0=sQuery(id+"F4.wireOp",EDGE,"E8");var subQ1=sQuery(id+"F4.wireOp",EDGE,"E5");var subQ2=makeQuery(id+"F4.imprint","INTERSECT",VERTEX,{"disambiguationData":[OD(0.0)],"derivedFrom":[subQ1,subQ0]});Q6=makeQuery(id+"F4.imprint","IMPRINT",FACE,{"disambiguationData":[TD([[makeQuery(id+"F4.imprint","IMPRINT",EDGE,{"disambiguationData":[TD([[subQ2,-1.0]])],"derivedFrom":subQ1}),1.0]])]});}
            var Q7;
            {var subQ0=sQuery(id+"F4.wireOp",EDGE,"E8");var subQ1=sQuery(id+"F4.wireOp",EDGE,"E5");var subQ2=makeQuery(id+"F4.imprint","INTERSECT",VERTEX,{"disambiguationData":[OD(0.0)],"derivedFrom":[subQ1,subQ0]});Q7=makeQuery(id+"F4.imprint","IMPRINT",FACE,{"disambiguationData":[TD([[makeQuery(id+"F4.imprint","IMPRINT",EDGE,{"disambiguationData":[TD([[subQ2,1.0]])],"derivedFrom":subQ1}),1.0]])]});}
            var Q8;
            {var subQ0=sQuery(id+"F4.wireOp",EDGE,"E8");var subQ1=sQuery(id+"F4.wireOp",EDGE,"E3");var subQ2=makeQuery(id+"F4.imprint","INTERSECT",VERTEX,{"disambiguationData":[OD(0.0)],"derivedFrom":[subQ1,subQ0]});Q8=makeQuery(id+"F4.imprint","IMPRINT",FACE,{"disambiguationData":[TD([[makeQuery(id+"F4.imprint","IMPRINT",EDGE,{"disambiguationData":[TD([[subQ2,1.0]])],"derivedFrom":subQ1}),1.0]])]});}
            var Q9;
            {var subQ0=sQuery(id+"F4.wireOp",EDGE,"E10");var subQ1=sQuery(id+"F4.wireOp",EDGE,"E3");var subQ2=makeQuery(id+"F4.imprint","INTERSECT",VERTEX,{"derivedFrom":[subQ1,subQ0]});Q9=makeQuery(id+"F4.imprint","IMPRINT",FACE,{"disambiguationData":[TD([[makeQuery(id+"F4.imprint","IMPRINT",EDGE,{"disambiguationData":[TD([[subQ2,-1.0]])],"derivedFrom":subQ1}),1.0]])]});}
            var Q10;
            {var subQ0=sQuery(id+"F4.wireOp",EDGE,"E10");var subQ1=sQuery(id+"F4.wireOp",EDGE,"E3");var subQ2=makeQuery(id+"F4.imprint","INTERSECT",VERTEX,{"derivedFrom":[subQ1,subQ0]});Q10=makeQuery(id+"F4.imprint","IMPRINT",FACE,{"disambiguationData":[TD([[makeQuery(id+"F4.imprint","IMPRINT",EDGE,{"disambiguationData":[TD([[subQ2,1.0]])],"derivedFrom":subQ1}),1.0]])]});}
            var Q11;
            {var subQ0=sQuery(id+"F4.wireOp",EDGE,"E10");var subQ1=sQuery(id+"F4.wireOp",EDGE,"E4");var subQ2=makeQuery(id+"F4.imprint","INTERSECT",VERTEX,{"disambiguationData":[OD(0.0)],"derivedFrom":[subQ1,subQ0]});Q11=makeQuery(id+"F4.imprint","IMPRINT",FACE,{"disambiguationData":[TD([[makeQuery(id+"F4.imprint","IMPRINT",EDGE,{"disambiguationData":[TD([[subQ2,1.0]])],"derivedFrom":subQ1}),1.0]])]});}
            var Q12;
            {var subQ0=sQuery(id+"F4.wireOp",EDGE,"E10");var subQ1=sQuery(id+"F4.wireOp",EDGE,"E4");var subQ2=makeQuery(id+"F4.imprint","INTERSECT",VERTEX,{"disambiguationData":[OD(0.0)],"derivedFrom":[subQ1,subQ0]});Q12=makeQuery(id+"F4.imprint","IMPRINT",FACE,{"disambiguationData":[TD([[makeQuery(id+"F4.imprint","IMPRINT",EDGE,{"disambiguationData":[TD([[subQ2,-1.0]])],"derivedFrom":subQ1}),1.0]])]});}
            var Q13;
            {var subQ0=sQuery(id+"F4.wireOp",EDGE,"E10");var subQ1=sQuery(id+"F4.wireOp",EDGE,"E2");var subQ2=makeQuery(id+"F4.imprint","INTERSECT",VERTEX,{"derivedFrom":[subQ1,subQ0]});Q13=makeQuery(id+"F4.imprint","IMPRINT",FACE,{"disambiguationData":[TD([[makeQuery(id+"F4.imprint","IMPRINT",EDGE,{"disambiguationData":[TD([[subQ2,-1.0]])],"derivedFrom":subQ1}),1.0]])]});}
            var Q14;
            {var subQ0=sQuery(id+"F4.wireOp",EDGE,"E10");var subQ1=sQuery(id+"F4.wireOp",EDGE,"E2");var subQ2=makeQuery(id+"F4.imprint","INTERSECT",VERTEX,{"derivedFrom":[subQ1,subQ0]});Q14=makeQuery(id+"F4.imprint","IMPRINT",FACE,{"disambiguationData":[TD([[makeQuery(id+"F4.imprint","IMPRINT",EDGE,{"disambiguationData":[TD([[subQ2,1.0]])],"derivedFrom":subQ1}),1.0]])]});}
            var Q15;
            {var subQ0=sQuery(id+"F4.wireOp",EDGE,"E9");var subQ1=sQuery(id+"F4.wireOp",EDGE,"E2");var subQ2=makeQuery(id+"F4.imprint","INTERSECT",VERTEX,{"disambiguationData":[OD(0.0)],"derivedFrom":[subQ1,subQ0]});Q15=makeQuery(id+"F4.imprint","IMPRINT",FACE,{"disambiguationData":[TD([[makeQuery(id+"F4.imprint","IMPRINT",EDGE,{"disambiguationData":[TD([[subQ2,1.0]])],"derivedFrom":subQ1}),1.0]])]});}
            extrude(context, id + "F14", {"entities" : qUnion([Q0, Q1, Q2, Q3, Q4, Q5, Q6, Q7, Q8, Q9, Q10, Q11, Q12, Q13, Q14, Q15]), "operationType" : NewBodyOperationType.REMOVE, "depth" : (getVariable(context, 'Extrude')) * mm});
        }
        {
            var Q0;
            Q0=makeQuery(id+"F2.opExtrude","CAP_EDGE",EDGE,{"disambiguationData":[OSD([sQuery(id+"F1.wireOp",EDGE,"E0.bottom")])],"isStart":true});
            var Q1;
            Q1=makeQuery(id+"F2.opExtrude","SWEPT_EDGE",EDGE,{"disambiguationData":[OSD([sQuery(id+"F1.wireOp",EDGE,"E0.bottom"),sQuery(id+"F1.wireOp",EDGE,"E0.left")])]});
            var Q2;
            Q2=makeQuery(id+"F2.opExtrude","CAP_EDGE",EDGE,{"disambiguationData":[OSD([sQuery(id+"F1.wireOp",EDGE,"E0.left")])],"isStart":true});
            var Q3;
            Q3=makeQuery(id+"F2.opExtrude","CAP_EDGE",EDGE,{"disambiguationData":[OSD([sQuery(id+"F1.wireOp",EDGE,"E0.bottom")])],"isStart":false});
            var Q4;
            Q4=makeQuery(id+"F2.opExtrude","CAP_EDGE",EDGE,{"disambiguationData":[OSD([sQuery(id+"F1.wireOp",EDGE,"E0.left")])],"isStart":false});
            var Q5;
            Q5=makeQuery(id+"F2.opExtrude","SWEPT_EDGE",EDGE,{"disambiguationData":[OSD([sQuery(id+"F1.wireOp",EDGE,"E0.bottom"),sQuery(id+"F1.wireOp",EDGE,"E0.right")])]});
            var Q6;
            Q6=makeQuery(id+"F2.opExtrude","CAP_EDGE",EDGE,{"disambiguationData":[OSD([sQuery(id+"F1.wireOp",EDGE,"E0.right")])],"isStart":false});
            var Q7;
            Q7=makeQuery(id+"F2.opExtrude","SWEPT_EDGE",EDGE,{"disambiguationData":[OSD([sQuery(id+"F1.wireOp",EDGE,"E0.top"),sQuery(id+"F1.wireOp",EDGE,"E0.right")])]});
            var Q8;
            Q8=makeQuery(id+"F2.opExtrude","CAP_EDGE",EDGE,{"disambiguationData":[OSD([sQuery(id+"F1.wireOp",EDGE,"E0.right")])],"isStart":true});
            var Q9;
            Q9=makeQuery(id+"F2.opExtrude","CAP_EDGE",EDGE,{"disambiguationData":[OSD([sQuery(id+"F1.wireOp",EDGE,"E0.top")])],"isStart":true});
            var Q10;
            Q10=makeQuery(id+"F2.opExtrude","CAP_EDGE",EDGE,{"disambiguationData":[OSD([sQuery(id+"F1.wireOp",EDGE,"E0.top")])],"isStart":false});
            var Q11;
            Q11=makeQuery(id+"F2.opExtrude","SWEPT_EDGE",EDGE,{"disambiguationData":[OSD([sQuery(id+"F1.wireOp",EDGE,"E0.top"),sQuery(id+"F1.wireOp",EDGE,"E0.left")])]});
            fillet(context, id + "F15", {"entities" : qUnion([Q0, Q1, Q2, Q3, Q4, Q5, Q6, Q7, Q8, Q9, Q10, Q11]), "radius" : 1.5 * mm, "tangentPropagation" : true, "allowEdgeOverflow" : false});
        }
    });
